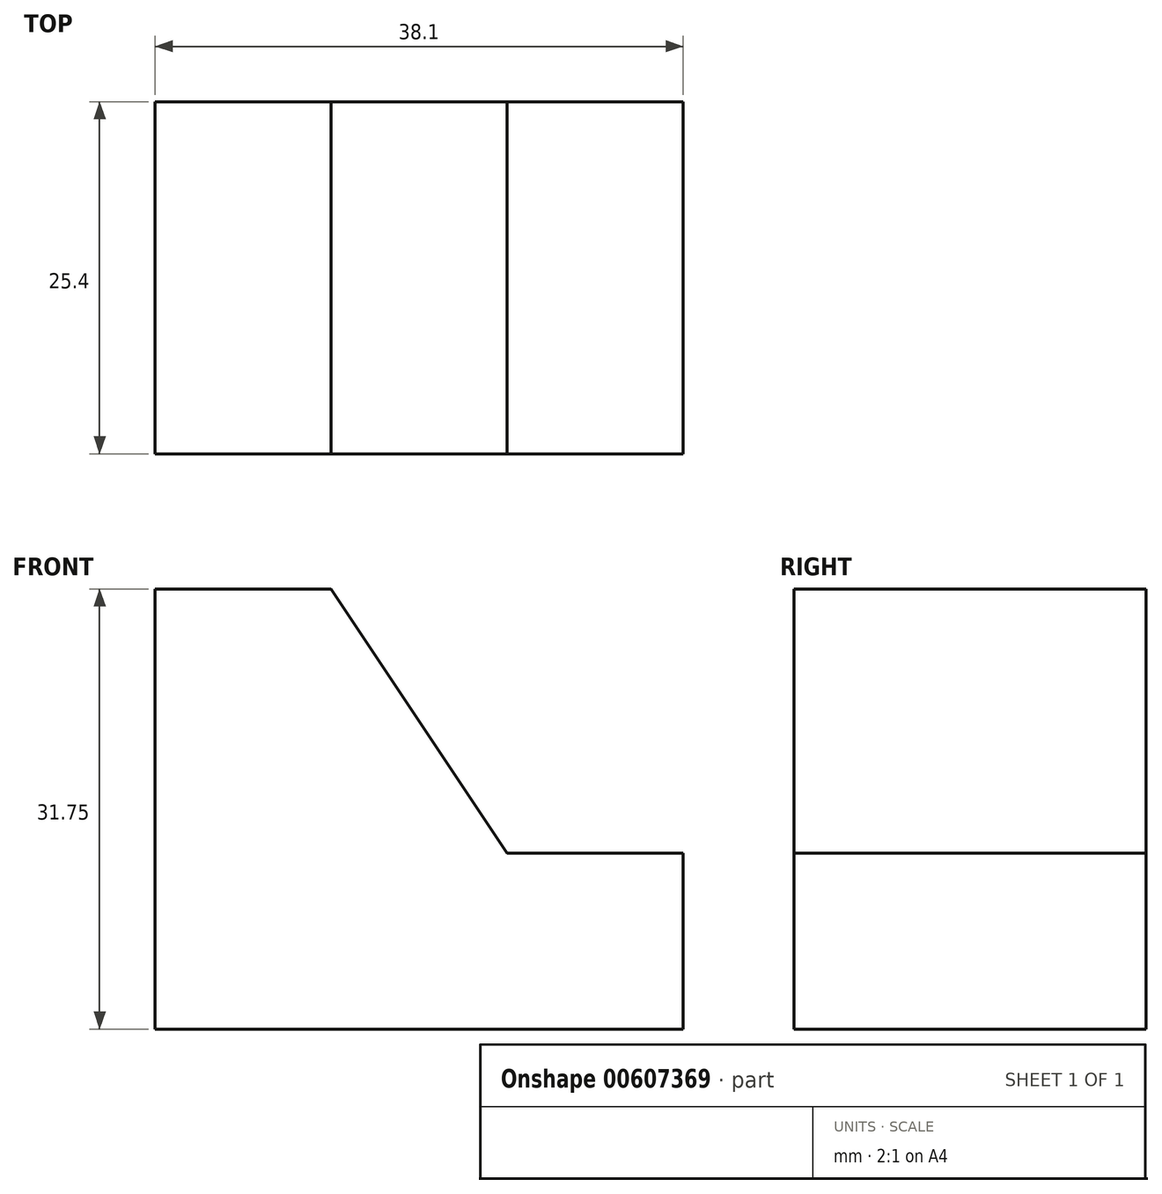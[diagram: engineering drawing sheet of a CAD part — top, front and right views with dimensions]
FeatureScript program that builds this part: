
annotation { "Feature Type Name" : "Feature", "Feature Type Description" : "" }
export const myFeature = defineFeature(function(context is Context, id is Id, definition is map)
    precondition{}
    {
        {
            var Q0;
            Q0=qCreatedBy(makeId("Front.planeOp"),FACE);
            var sketch = newSketch(context, id + "F0", { "sketchPlane" : qUnion([Q0])});
            skLineSegment(sketch, "E0", {"start": v(0, 0) * mm, "end": v(0, 31.75) * mm});
            skLineSegment(sketch, "E1", {"start": v(0, 31.75) * mm, "end": v(12.7, 31.75) * mm});
            skLineSegment(sketch, "E2", {"start": v(0, 0) * mm, "end": v(38.1, 0) * mm});
            skLineSegment(sketch, "E3", {"start": v(38.1, 0) * mm, "end": v(38.1, 12.7) * mm});
            skLineSegment(sketch, "E4", {"start": v(38.1, 12.7) * mm, "end": v(25.4, 12.7) * mm});
            skLineSegment(sketch, "E5", {"start": v(12.7, 31.75) * mm, "end": v(25.4, 12.7) * mm});
            skSolve(sketch);
        }
        {
            var Q0;
            Q0 = qSketchRegion(id + "F0", true);
            extrude(context, id + "F1", {"entities" : qUnion([Q0]), "depth" : 25.4 * mm, "offsetDistance" : 25.4 * mm});
        }
    });
